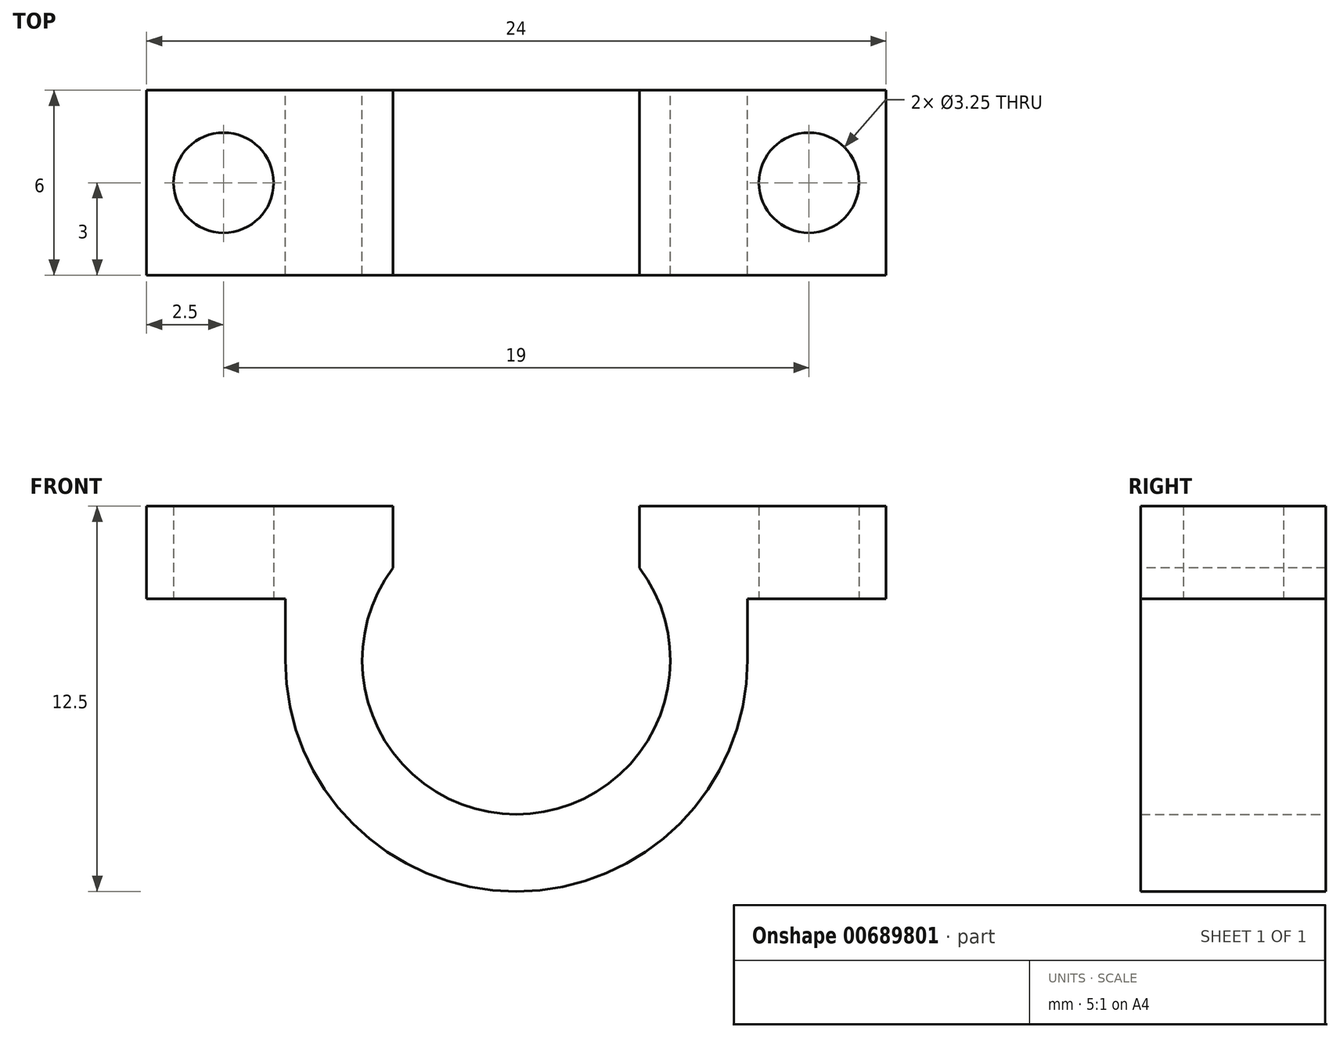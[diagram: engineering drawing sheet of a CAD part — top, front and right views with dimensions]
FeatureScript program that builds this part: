
annotation { "Feature Type Name" : "Feature", "Feature Type Description" : "" }
export const myFeature = defineFeature(function(context is Context, id is Id, definition is map)
    precondition{}
    {
        {
            var Q0;
            Q0=qCreatedBy(makeId("Top.planeOp"),FACE);
            var sketch = newSketch(context, id + "F0", { "sketchPlane" : qUnion([Q0])});
            skCircle(sketch, "E0", {"center": v(-9.5, 0) * mm, "radius": 1.63 * mm});
            skCircle(sketch, "E1", {"center": v(9.5, 0) * mm, "radius": 1.63 * mm});
            skLineSegment(sketch, "E2.bottom", {"start": v(-12, 3) * mm, "end": v(12, 3) * mm});
            skLineSegment(sketch, "E2.top", {"start": v(-12, -3) * mm, "end": v(12, -3) * mm});
            skLineSegment(sketch, "E2.left", {"start": v(-12, 3) * mm, "end": v(-12, -3) * mm});
            skLineSegment(sketch, "E2.right", {"start": v(12, 3) * mm, "end": v(12, -3) * mm});
            skSolve(sketch);
        }
        {
            var Q0;
            Q0=makeQuery(id+"F0.imprint","IMPRINT",FACE,{"disambiguationData":[TD([[makeQuery(id+"F0.imprint","IMPRINT",EDGE,{"derivedFrom":sQuery(id+"F0.wireOp",EDGE,"E0")}),-1.0]])]});
            extrude(context, id + "F1", {"entities" : qUnion([Q0]), "depth" : 3 * mm, "offsetDistance" : 25 * mm});
        }
        {
            var Q0;
            Q0=makeQuery(id+"F1.opExtrude","SWEPT_FACE",FACE,{"disambiguationData":[OSD([sQuery(id+"F0.wireOp",EDGE,"E2.bottom")])]});
            var sketch = newSketch(context, id + "F2", { "sketchPlane" : qUnion([Q0])});
            skArc(sketch, "E3", {"start": v(-7.5, -2) * mm, "mid": v(0, -9.5) * mm, "end": v(7.5, -2) * mm});
            skLineSegment(sketch, "E4", {"start": v(-7.5, -2) * mm, "end": v(-7.5, 0) * mm});
            skLineSegment(sketch, "E5", {"start": v(-4.74, 3.81) * mm, "end": v(-4.74, 3.81) * mm});
            skLineSegment(sketch, "E6", {"start": v(7.5, -2) * mm, "end": v(7.5, 0) * mm});
            skCircle(sketch, "E7", {"center": v(0, -2) * mm, "radius": 5 * mm});
            skSolve(sketch);
        }
        {
            var Q0;
            Q0=makeQuery(id+"F2.imprint","IMPRINT",FACE,{"disambiguationData":[TD([[makeQuery(id+"F2.imprint","IMPRINT",EDGE,{"derivedFrom":sQuery(id+"F2.wireOp",EDGE,"E3")}),1.0]])]});
            extrude(context, id + "F3", {"entities" : qUnion([Q0]), "operationType" : NewBodyOperationType.ADD, "depth" : -6 * mm, "offsetDistance" : 25 * mm});
        }
        {
            var Q0;
            Q0=makeQuery(id+"F3.boolean.opBoolean","MERGE",FACE,{"derivedFrom":[makeQuery(id+"F1.opExtrude","SWEPT_FACE",FACE,{"disambiguationData":[OSD([sQuery(id+"F0.wireOp",EDGE,"E2.top")])]}),makeQuery(id+"F3.opExtrude","CAP_FACE",FACE,{"disambiguationData":[OSD([sQuery(id+"F0.wireOp",EDGE,"E2.bottom"),sQuery(id+"F2.wireOp",EDGE,"E3"),sQuery(id+"F2.wireOp",EDGE,"E4"),sQuery(id+"F2.wireOp",EDGE,"E6"),sQuery(id+"F2.wireOp",EDGE,"E7")])],"isStart":false})]});
            var sketch = newSketch(context, id + "F4", { "sketchPlane" : qUnion([Q0])});
            skLineSegment(sketch, "E8", {"start": v(-4, -1.4) * mm, "end": v(-4, 3) * mm});
            skLineSegment(sketch, "E9", {"start": v(-4, 3) * mm, "end": v(4, 3) * mm});
            skLineSegment(sketch, "E10", {"start": v(4, 3) * mm, "end": v(4, -1.45) * mm});
            skLineSegment(sketch, "E11", {"start": v(4, -1.45) * mm, "end": v(-4, -1.4) * mm});
            skCircle(sketch, "E12", {"center": v(0, -2) * mm, "radius": 5 * mm});
            skSolve(sketch);
        }
        {
            var Q0;
            {var subQ0=sQuery(id+"F4.wireOp",EDGE,"E9");var subQ1=sQuery(id+"F4.wireOp",EDGE,"E8");var subQ3=sQuery(id+"F4.wireOp",EDGE,"E12");var subQ4=makeQuery(id+"F4.imprint","INTERSECT",VERTEX,{"derivedFrom":[subQ1,subQ3]});var subQ5=makeQuery(id+"F4.imprint","INTERSECT",VERTEX,{"derivedFrom":[subQ0,subQ3]});Q0=makeQuery(id+"F4.imprint","IMPRINT",FACE,{"disambiguationData":[TD([[makeQuery(id+"F4.imprint","IMPRINT",EDGE,{"disambiguationData":[TD([[subQ5,-1.0],[subQ4,1.0]])],"derivedFrom":subQ3}),-1.0]])]});}
            var Q1;
            {var subQ0=sQuery(id+"F4.wireOp",EDGE,"E12");var subQ1=sQuery(id+"F4.wireOp",EDGE,"E8");var subQ2=makeQuery(id+"F4.imprint","INTERSECT",VERTEX,{"derivedFrom":[subQ1,subQ0]});Q1=makeQuery(id+"F4.imprint","IMPRINT",FACE,{"disambiguationData":[TD([[makeQuery(id+"F4.imprint","IMPRINT",EDGE,{"disambiguationData":[TD([[subQ2,1.0]])],"derivedFrom":subQ1}),1.0]])]});}
            var Q2;
            {var subQ0=sQuery(id+"F4.wireOp",EDGE,"E12");var subQ1=makeQuery(id+"F4.imprint","INTERSECT",VERTEX,{"derivedFrom":[sQuery(id+"F4.wireOp",EDGE,"E9"),subQ0]});var subQ2=sQuery(id+"F4.wireOp",EDGE,"E10");var subQ3=makeQuery(id+"F4.imprint","INTERSECT",VERTEX,{"derivedFrom":[subQ2,subQ0]});Q2=makeQuery(id+"F4.imprint","IMPRINT",FACE,{"disambiguationData":[TD([[makeQuery(id+"F4.imprint","IMPRINT",EDGE,{"disambiguationData":[TD([[subQ1,1.0],[subQ3,-1.0]])],"derivedFrom":subQ0}),1.0]])]});}
            var Q3;
            {var subQ0=sQuery(id+"F4.wireOp",EDGE,"E10");var subQ1=sQuery(id+"F4.wireOp",EDGE,"E9");var subQ3=sQuery(id+"F4.wireOp",EDGE,"E12");var subQ4=makeQuery(id+"F4.imprint","INTERSECT",VERTEX,{"derivedFrom":[subQ1,subQ3]});var subQ5=makeQuery(id+"F4.imprint","INTERSECT",VERTEX,{"derivedFrom":[subQ0,subQ3]});Q3=makeQuery(id+"F4.imprint","IMPRINT",FACE,{"disambiguationData":[TD([[makeQuery(id+"F4.imprint","IMPRINT",EDGE,{"disambiguationData":[TD([[subQ4,1.0],[subQ5,-1.0]])],"derivedFrom":subQ3}),-1.0]])]});}
            var Q4;
            {var subQ0=sQuery(id+"F4.wireOp",EDGE,"E12");var subQ1=sQuery(id+"F4.wireOp",EDGE,"E10");var subQ2=makeQuery(id+"F4.imprint","INTERSECT",VERTEX,{"derivedFrom":[subQ1,subQ0]});Q4=makeQuery(id+"F4.imprint","IMPRINT",FACE,{"disambiguationData":[TD([[makeQuery(id+"F4.imprint","IMPRINT",EDGE,{"disambiguationData":[TD([[subQ2,-1.0]])],"derivedFrom":subQ1}),1.0]])]});}
            extrude(context, id + "F5", {"entities" : qUnion([Q0, Q1, Q2, Q3, Q4]), "operationType" : NewBodyOperationType.REMOVE, "endBound" : BoundingType.THROUGH_ALL, "oppositeDirection" : true, "depth" : 25 * mm, "offsetDistance" : 25 * mm});
        }
    });
